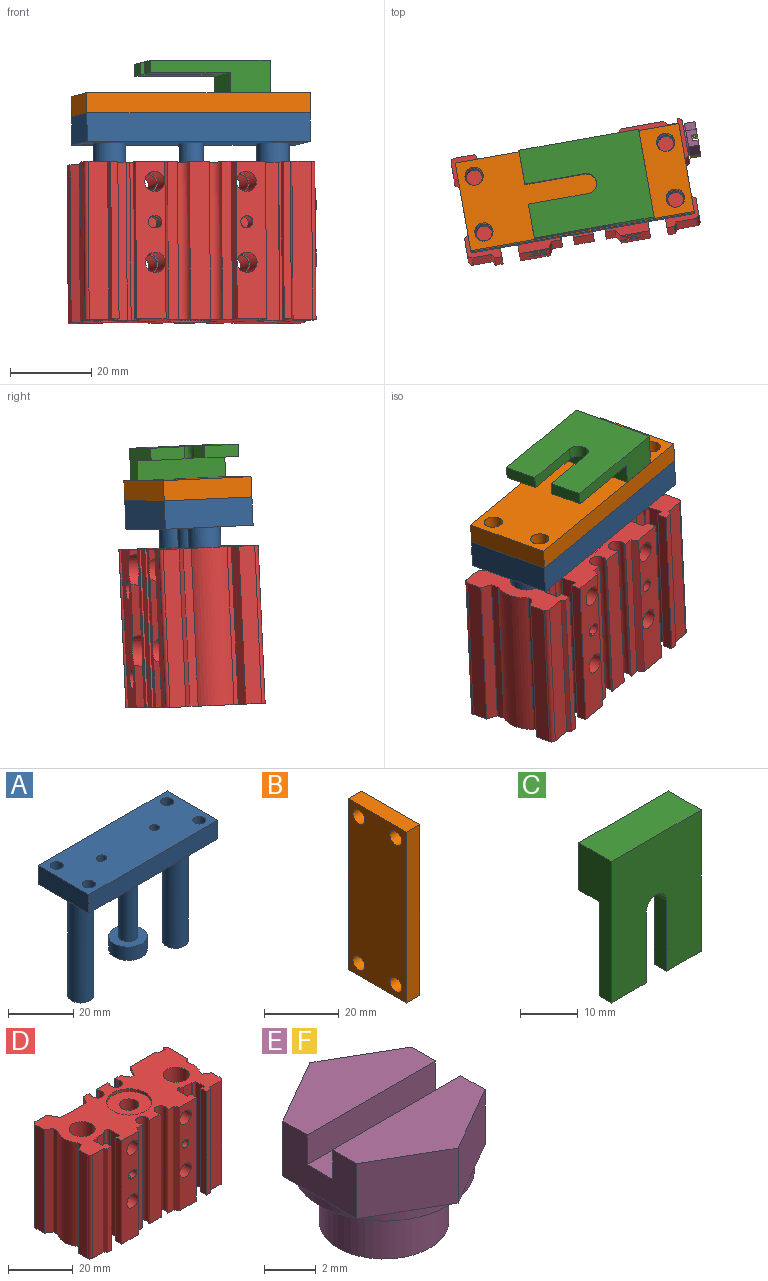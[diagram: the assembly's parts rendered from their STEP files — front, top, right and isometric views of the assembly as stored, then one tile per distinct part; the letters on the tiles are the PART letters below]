
ASSEMBLY  parts=6 mates=5
PART A: 30 faces, bbox 56x22x47.5 mm
  f0: plane 22x7mm, normal (-1,0,0), area 154mm2, adj f1,f3,f4,f5
  f1: plane 56x7mm, normal (0,-1,0), area 392mm2, adj f0,f2,f4,f5
  f2: plane 22x7mm, normal (1,0,0), area 154mm2, adj f1,f3,f4,f5
  f3: plane 56x7mm, normal (0,1,0), area 392mm2, adj f0,f2,f4,f5
  f4: plane 56x22mm, normal (0,0,1), area 1166.1mm2, adj f0,f1,f2,f3,f14,f18,f19,f20
  f5: plane 56x22mm, normal (0,0,-1), area 1052.9mm2, adj f0,f1,f2,f3,f6,f10,f12,f18
  f6: cylinder r=3mm len=28mm, axis (0,0,1), area 527.8mm2, adj f5,f8
  f7: cylinder r=5.95mm len=11.9mm, axis (0,0,-1), area 186.9mm2, adj f8,f9
  f8: plane 11.9x11.9mm, normal (0,0,1), area 82.9mm2, adj f6,f7
  f9: plane 11.9x11.9mm, normal (0,0,-1), area 111.2mm2, adj f7
  f10: cylinder r=4mm len=40mm, axis (0,0,1), area 1005.3mm2, adj f5,f16
  f11: plane 7x7mm, normal (0,0,-1), area 38.5mm2, adj f16
  f12: cylinder r=4mm len=40mm, axis (0,0,1), area 1005.3mm2, adj f5,f17
  f13: plane 7x7mm, normal (0,0,-1), area 38.5mm2, adj f17
  f14: cylinder r=1.5mm len=6mm, axis (0,0,1), area 56.5mm2, adj f4,f15
  f15: plane 3x3mm, normal (0,0,1), area 7.1mm2, adj f14
  f16: cone r=3.5mm half-angle=45deg, axis (0,0,1), area 16.7mm2, adj f10,f11
  f17: cone r=3.5mm half-angle=45deg, axis (0,0,1), area 16.7mm2, adj f12,f13
  f18: cylinder r=2mm len=7mm, axis (0,0,1), area 88mm2, adj f4,f5
  f19: cylinder r=2mm len=7mm, axis (0,0,1), area 88mm2, adj f4,f5
  f20: cylinder r=2mm len=7mm, axis (0,0,1), area 88mm2, adj f4,f5
  f21: cylinder r=2mm len=7mm, axis (0,0,1), area 88mm2, adj f4,f5
  f22: plane 3x0.5mm, normal (0,1,0), area 1.5mm2, adj f4,f24,f25,f26,f27
  f23: plane 3x0.5mm, normal (0,-1,0), area 1.5mm2, adj f4,f24,f25,f26,f27
  f24: plane 3x1.75mm, normal (0,0,1), area 0.8mm2, adj f22,f23,f27,f29
  f25: plane 3x1.75mm, normal (0,0,1), area 0.8mm2, adj f22,f23,f26,f29
  f26: cylinder r=1.5mm len=3mm, axis (0,0,1), area 14.1mm2, adj f4,f22,f23,f25
  f27: cylinder r=1.5mm len=3mm, axis (0,0,1), area 14.1mm2, adj f4,f22,f23,f24
  f28: plane 3x3mm, normal (0,0,1), area 7.1mm2, adj f29
  f29: cylinder r=1.5mm len=3mm, axis (0,0,1), area 28.3mm2, adj f24,f25,f28
PART B: 10 faces, bbox 5x22x56 mm
  f0: plane 56x5mm, normal (0,-1,0), area 280mm2, adj f1,f3,f4,f5
  f1: plane 22x5mm, normal (0,0,-1), area 110mm2, adj f0,f2,f4,f5
  f2: plane 56x5mm, normal (0,1,0), area 280mm2, adj f1,f3,f4,f5
  f3: plane 22x5mm, normal (0,0,1), area 110mm2, adj f0,f2,f4,f5
  f4: plane 56x22mm, normal (1,0,0), area 1168.4mm2, adj f0,f1,f2,f3,f6,f7,f8,f9
  f5: plane 56x22mm, normal (-1,0,0), area 1168.4mm2, adj f0,f1,f2,f3,f6,f7,f8,f9
  f6: cylinder r=2.25mm len=5mm, axis (1,0,0), area 70.7mm2, adj f4,f5
  f7: cylinder r=2.25mm len=5mm, axis (1,0,0), area 70.7mm2, adj f4,f5
  f8: cylinder r=2.25mm len=5mm, axis (1,0,0), area 70.7mm2, adj f4,f5
  f9: cylinder r=2.25mm len=5mm, axis (1,0,0), area 70.7mm2, adj f4,f5
PART C: 12 faces, bbox 22x8x30 mm
  f0: plane 8.5x3mm, normal (0,0,-1), area 25.5mm2, adj f1,f2,f8,f11
  f1: plane 30x22mm, normal (0,-1,0), area 575.2mm2, adj f0,f3,f6,f7,f8,f9,f10,f11
  f2: plane 22x20mm, normal (0,1,0), area 355.2mm2, adj f0,f3,f4,f7,f8,f9,f10,f11
  f3: plane 8.5x3mm, normal (0,0,-1), area 25.5mm2, adj f1,f2,f7,f9
  f4: plane 22x5mm, normal (0,0,-1), area 110mm2, adj f2,f5,f7,f8
  f5: plane 22x10mm, normal (0,1,0), area 220mm2, adj f4,f6,f7,f8
  f6: plane 22x8mm, normal (0,0,1), area 176mm2, adj f1,f5,f7,f8
  f7: plane 30x8mm, normal (1,0,0), area 140mm2, adj f1,f2,f3,f4,f5,f6
  f8: plane 30x8mm, normal (-1,0,0), area 140mm2, adj f0,f1,f2,f4,f5,f6
  f9: plane 15x3mm, normal (-1,0,0), area 45mm2, adj f1,f2,f3,f10
  f10: cylinder r=2.5mm len=5mm, axis (0,-1,0), area 23.6mm2, adj f1,f2,f9,f11
  f11: plane 15x3mm, normal (1,0,0), area 45mm2, adj f0,f1,f2,f10
PART D: 162 faces, bbox 58x26x39 mm
  f0: plane 12x12mm, normal (0,0,1), area 113.1mm2, adj f1
  f1: cylinder r=6mm len=15mm, axis (0,0,1), area 565.5mm2, adj f0,f2
  f2: plane 12x12mm, normal (0,0,-1), area 84.8mm2, adj f1,f3
  f3: cylinder r=3mm len=11mm, axis (0,0,1), area 207.3mm2, adj f2,f92
  f4: plane 4x2.31mm, normal (-0.87,0.5,0), area 5.3mm2, adj f6,f14,f83,f121
  f5: plane 13.07x4mm, normal (-0.87,0.5,0), area 56.8mm2, adj f7,f83,f116,f121
  f6: plane 1.52x1.44mm, normal (0,1,0), area 1.8mm2, adj f4,f14,f86,f121
  f7: plane 12.88x1.52mm, normal (0,1,0), area 18.7mm2, adj f5,f8,f116,f121
  f8: plane 16.13x2.9mm, normal (0.87,0.5,0), area 47.5mm2, adj f7,f17,f116,f121
  f9: plane 12.06x2.9mm, normal (0.87,0.5,0), area 37.1mm2, adj f13,f17,f85,f116
  f10: plane 16.13x2.9mm, normal (-0.87,0.5,0), area 47.5mm2, adj f87,f89,f106,f111
  f11: plane 3.06x2.9mm, normal (-0.87,0.5,0), area 7mm2, adj f14,f87,f89,f106
  f12: plane 39x2.5mm, normal (0,-1,0), area 97.5mm2, adj f13,f14,f54,f104
  f13: plane 58x26mm, normal (0,0,-1), area 919.8mm2, adj f9,f12,f15,f16,f17,f18,f20,f22
  f14: plane 58x26mm, normal (0,0,1), area 947.9mm2, adj f4,f6,f11,f12,f15,f16,f17,f30
  f15: plane 39x2.5mm, normal (0,-1,0), area 97.5mm2, adj f13,f14,f56,f100
  f16: plane 39x5mm, normal (0,1,0), area 195mm2, adj f13,f14,f95,f97
  f17: plane 39x2.5mm, normal (0,1,0), area 94.9mm2, adj f8,f9,f13,f14,f86,f98,f116,f121
  f18: cylinder r=6mm len=12mm, axis (0,0,-1), area 37.7mm2, adj f13,f19
  f19: plane 12x12mm, normal (0,0,-1), area 113.1mm2, adj f18
  f20: cylinder r=1.5mm len=6mm, axis (0,0,-1), area 56.5mm2, adj f13,f21
  f21: plane 3x3mm, normal (0,0,-1), area 7.1mm2, adj f20
  f22: plane 3x1.5mm, normal (0,-1,0), area 4.5mm2, adj f13,f24,f25,f26,f27
  f23: plane 3x1.5mm, normal (0,1,0), area 4.5mm2, adj f13,f24,f25,f26,f27
  f24: plane 3x2.25mm, normal (0,0,-1), area 2.3mm2, adj f22,f23,f26,f29
  f25: plane 3x2.25mm, normal (0,0,-1), area 2.3mm2, adj f22,f23,f27,f29
  f26: cylinder r=1.5mm len=3mm, axis (0,0,-1), area 14.1mm2, adj f13,f22,f23,f24
  f27: cylinder r=1.5mm len=3mm, axis (0,0,-1), area 14.1mm2, adj f13,f22,f23,f25
  f28: plane 3x3mm, normal (0,0,-1), area 7.1mm2, adj f29
  f29: cylinder r=1.5mm len=3mm, axis (0,0,-1), area 28.3mm2, adj f24,f25,f28
  f30: cylinder r=1mm len=39mm, axis (0,0,1), area 61.3mm2, adj f13,f14,f31,f91
  f31: plane 39x4mm, normal (-1,0,0), area 156mm2, adj f13,f14,f30,f32
  f32: plane 39x2.5mm, normal (-0.5,-0.87,0), area 112.6mm2, adj f13,f14,f31,f33
  f33: plane 39x2.06mm, normal (-1,0,0), area 80.2mm2, adj f13,f14,f32,f34
  f34: cylinder r=7.5mm len=39mm, axis (0,0,1), area 376.4mm2, adj f13,f14,f33,f35
  f35: plane 39x1.06mm, normal (-1,0,0), area 41.2mm2, adj f13,f14,f34,f36
  f36: plane 39x2.5mm, normal (-0.5,0.87,0), area 112.6mm2, adj f13,f14,f35,f37
  f37: plane 39x4mm, normal (-1,0,0), area 156mm2, adj f13,f14,f36,f38
  f38: cylinder r=1mm len=39mm, axis (0,0,1), area 61.3mm2, adj f13,f14,f37,f39
  f39: plane 39x4.92mm, normal (0,-1,0), area 192mm2, adj f13,f14,f38,f40
  f40: plane 39x1mm, normal (-0.87,-0.5,0), area 45mm2, adj f13,f14,f39,f41
  f41: plane 39x1.8mm, normal (0,-1,0), area 70.2mm2, adj f13,f14,f40,f42
  f42: plane 39x2.5mm, normal (1,0,0), area 97.5mm2, adj f13,f14,f41,f43
  f43: plane 39x1.5mm, normal (0,1,0), area 58.5mm2, adj f13,f14,f42,f44
  f44: plane 39x3.7mm, normal (1,0,0), area 144.3mm2, adj f13,f14,f43,f45
  f45: plane 39x1.5mm, normal (0,-1,0), area 58.5mm2, adj f13,f14,f44,f46
  f46: plane 39x0.5mm, normal (1,0,0), area 19.5mm2, adj f13,f14,f45,f47
  f47: plane 39x3.25mm, normal (0,-1,0), area 126.8mm2, adj f13,f14,f46,f48
  f48: cylinder r=7mm len=39mm, axis (0,0,1), area 48.3mm2, adj f13,f14,f47,f49
  f49: cylinder r=1mm len=39mm, axis (0,0,1), area 85.8mm2, adj f13,f14,f48,f50
  f50: plane 39x4.03mm, normal (-1,0,0), area 157mm2, adj f13,f14,f49,f51
  f51: plane 39x1.5mm, normal (0,1,0), area 58.5mm2, adj f13,f14,f50,f52
  f52: plane 39x2.5mm, normal (-1,0,0), area 97.5mm2, adj f13,f14,f51,f53
  f53: plane 39x7.38mm, normal (0,-1,0), area 239.8mm2, adj f13,f14,f52,f54,f110,f115,f128,f129
  f54: plane 39x1.6mm, normal (0.87,-0.5,0), area 72.1mm2, adj f12,f13,f14,f53
  f55: plane 39x5mm, normal (0,-1,0), area 195mm2, adj f13,f14,f101,f103
  f56: plane 39x1.6mm, normal (-0.87,-0.5,0), area 72.1mm2, adj f13,f14,f15,f57
  f57: plane 39x7.38mm, normal (0,-1,0), area 241.3mm2, adj f13,f14,f56,f58,f120,f125,f126
  f58: plane 39x2.5mm, normal (1,0,0), area 97.5mm2, adj f13,f14,f57,f59
  f59: plane 39x1.5mm, normal (0,1,0), area 58.5mm2, adj f13,f14,f58,f60
  f60: plane 39x4.03mm, normal (1,0,0), area 157mm2, adj f13,f14,f59,f61
  f61: cylinder r=1mm len=39mm, axis (0,0,1), area 85.8mm2, adj f13,f14,f60,f62
  f62: cylinder r=7mm len=39mm, axis (0,0,1), area 48.3mm2, adj f13,f14,f61,f63
  f63: plane 39x3.25mm, normal (0,-1,0), area 126.8mm2, adj f13,f14,f62,f64
  f64: plane 39x0.5mm, normal (-1,0,0), area 19.5mm2, adj f13,f14,f63,f65
  f65: plane 39x1.5mm, normal (0,-1,0), area 58.5mm2, adj f13,f14,f64,f66
  f66: plane 39x3.7mm, normal (-1,0,0), area 144.3mm2, adj f13,f14,f65,f67
  f67: plane 39x1.5mm, normal (0,1,0), area 58.5mm2, adj f13,f14,f66,f68
  f68: plane 39x2.5mm, normal (-1,0,0), area 97.5mm2, adj f13,f14,f67,f69
  f69: plane 39x1.8mm, normal (0,-1,0), area 70.2mm2, adj f13,f14,f68,f70
  f70: plane 39x1mm, normal (0.87,-0.5,0), area 45mm2, adj f13,f14,f69,f71
  f71: plane 39x4.92mm, normal (0,-1,0), area 192mm2, adj f13,f14,f70,f72
  f72: cylinder r=1mm len=39mm, axis (0,0,1), area 61.3mm2, adj f13,f14,f71,f73
  f73: plane 39x4mm, normal (1,0,0), area 156mm2, adj f13,f14,f72,f74
  f74: plane 39x2.5mm, normal (0.5,0.87,0), area 112.6mm2, adj f13,f14,f73,f75
  f75: plane 39x1.06mm, normal (1,0,0), area 41.2mm2, adj f13,f14,f74,f76
  f76: cylinder r=7.5mm len=39mm, axis (0,0,1), area 293.6mm2, adj f13,f14,f75,f77
  f77: plane 39x1.48mm, normal (0.5,-0.87,0), area 66.7mm2, adj f13,f14,f76,f78
  f78: plane 39x8.5mm, normal (1,0,0), area 292.2mm2, adj f13,f14,f77,f79,f155,f159
  f79: cylinder r=1mm len=39mm, axis (0,0,1), area 61.3mm2, adj f13,f14,f78,f80
  f80: plane 39x1mm, normal (-0.94,0.34,0), area 41.5mm2, adj f13,f14,f79,f81
  f81: plane 39x2.44mm, normal (0,1,0), area 95mm2, adj f13,f14,f80,f82
  f82: plane 39x1mm, normal (0.82,0.57,0), area 47.6mm2, adj f13,f14,f81,f83
  f83: plane 39x11mm, normal (0,1,0), area 370.1mm2, adj f4,f5,f13,f14,f82,f84,f116,f121
  f84: plane 10.54x4mm, normal (-0.87,0.5,0), area 46.9mm2, adj f13,f83,f85,f116
  f85: plane 10.44x1.52mm, normal (0,1,0), area 15.4mm2, adj f9,f13,f84,f116
  f86: plane 3.06x2.9mm, normal (0.87,0.5,0), area 7mm2, adj f6,f14,f17,f121
  f87: plane 39x2.5mm, normal (0,1,0), area 94.9mm2, adj f10,f11,f13,f14,f88,f94,f106,f111
  f88: plane 12.06x2.9mm, normal (-0.87,0.5,0), area 37.1mm2, adj f13,f87,f89,f111
  f89: plane 39x11.02mm, normal (0,1,0), area 351.2mm2, adj f10,f11,f13,f14,f88,f90,f106,f111
  f90: plane 39x4mm, normal (0.87,0.5,0), area 180.1mm2, adj f13,f14,f89,f91
  f91: plane 39x5mm, normal (0,1,0), area 195mm2, adj f13,f14,f30,f90
  f92: plane 14x14mm, normal (0,0,1), area 125.7mm2, adj f3,f93
  f93: cylinder r=7mm len=14mm, axis (0,0,1), area 44mm2, adj f14,f92
  f94: plane 39x0.74mm, normal (1,0,0), area 28.8mm2, adj f13,f14,f87,f96
  f95: plane 39x0.74mm, normal (-1,0,0), area 28.8mm2, adj f13,f14,f16,f96
  f96: cylinder r=2.02mm len=39mm, axis (0,0,1), area 364.5mm2, adj f13,f14,f94,f95
  f97: plane 39x0.74mm, normal (1,0,0), area 28.8mm2, adj f13,f14,f16,f99
  f98: plane 39x0.74mm, normal (-1,0,0), area 28.8mm2, adj f13,f14,f17,f99
  f99: cylinder r=2.02mm len=39mm, axis (0,0,1), area 364.5mm2, adj f13,f14,f97,f98
  f100: plane 39x0.24mm, normal (-1,0,0), area 9.3mm2, adj f13,f14,f15,f102
  f101: plane 39x0.24mm, normal (1,0,0), area 9.3mm2, adj f13,f14,f55,f102
  f102: cylinder r=2.02mm len=39mm, axis (0,0,1), area 364.5mm2, adj f13,f14,f100,f101
  f103: plane 39x0.24mm, normal (-1,0,0), area 9.3mm2, adj f13,f14,f55,f105
  f104: plane 39x0.24mm, normal (1,0,0), area 9.3mm2, adj f12,f13,f14,f105
  f105: cylinder r=2.02mm len=39mm, axis (0,0,1), area 364.5mm2, adj f13,f14,f103,f104
  f106: cylinder r=4mm len=8mm, axis (0,1,0), area 31.8mm2, adj f10,f11,f87,f89,f107
  f107: plane 8x8mm, normal (0,1,0), area 35.7mm2, adj f106,f108
  f108: cylinder r=2.15mm len=11.5mm, axis (0,1,0), area 155.4mm2, adj f107,f109
  f109: plane 5x5mm, normal (0,-1,0), area 5.1mm2, adj f108,f110
  f110: cylinder r=2.5mm len=10mm, axis (0,1,0), area 157.1mm2, adj f53,f109
  f111: cylinder r=4mm len=8mm, axis (0,1,0), area 31.8mm2, adj f10,f87,f88,f89,f112
  f112: plane 8x8mm, normal (0,1,0), area 35.7mm2, adj f111,f113
  f113: cylinder r=2.15mm len=11.5mm, axis (0,1,0), area 155.4mm2, adj f112,f114
  f114: plane 5x5mm, normal (0,-1,0), area 5.1mm2, adj f113,f115
  f115: cylinder r=2.5mm len=10mm, axis (0,1,0), area 157.1mm2, adj f53,f114
  f116: cylinder r=4mm len=8mm, axis (0,1,0), area 75.2mm2, adj f5,f7,f8,f9,f17,f83,f84,f85
  f117: plane 8x8mm, normal (0,1,0), area 35.7mm2, adj f116,f118
  f118: cylinder r=2.15mm len=11.5mm, axis (0,1,0), area 155.4mm2, adj f117,f119
  f119: plane 5x5mm, normal (0,-1,0), area 5.1mm2, adj f118,f120
  f120: cylinder r=2.5mm len=10mm, axis (0,1,0), area 157.1mm2, adj f57,f119
  f121: cylinder r=4mm len=8mm, axis (0,1,0), area 75.2mm2, adj f4,f5,f6,f7,f8,f17,f83,f86
  f122: plane 8x8mm, normal (0,1,0), area 35.7mm2, adj f121,f123
  f123: cylinder r=2.15mm len=11.5mm, axis (0,1,0), area 155.4mm2, adj f122,f124
  f124: plane 5x5mm, normal (0,-1,0), area 5.1mm2, adj f123,f125
  f125: cylinder r=2.5mm len=10mm, axis (0,1,0), area 157.1mm2, adj f57,f124
  f126: cylinder r=1.5mm len=6mm, axis (0,-1,0), area 56.5mm2, adj f57,f127
  f127: plane 3x3mm, normal (0,-1,0), area 7.1mm2, adj f126
  f128: plane 3x0.5mm, normal (0,0,1), area 1.5mm2, adj f53,f130,f131,f132,f133
  f129: plane 3x0.5mm, normal (0,0,-1), area 1.5mm2, adj f53,f130,f131,f132,f133
  f130: plane 3x1.75mm, normal (0,-1,0), area 0.8mm2, adj f128,f129,f133,f135
  f131: plane 3x1.75mm, normal (0,-1,0), area 0.7mm2, adj f128,f129,f132,f135
  f132: cylinder r=1.5mm len=3mm, axis (0,-1,0), area 14.1mm2, adj f53,f128,f129,f131
  f133: cylinder r=1.5mm len=3mm, axis (0,-1,0), area 14.1mm2, adj f53,f128,f129,f130
  f134: plane 3x3mm, normal (0,-1,0), area 7.1mm2, adj f135
  f135: cylinder r=1.5mm len=3mm, axis (0,-1,0), area 28.3mm2, adj f130,f131,f134
  f136: cylinder r=2mm len=10mm, axis (0,0,-1), area 125.7mm2, adj f13,f137
  f137: plane 4x4mm, normal (0,0,-1), area 12.6mm2, adj f136
  f138: cylinder r=2mm len=10mm, axis (0,0,-1), area 125.7mm2, adj f13,f139
  f139: plane 4x4mm, normal (0,0,-1), area 12.6mm2, adj f138
  f140: cylinder r=2mm len=10mm, axis (0,0,-1), area 125.7mm2, adj f13,f141
  f141: plane 4x4mm, normal (0,0,-1), area 12.6mm2, adj f140
  f142: cylinder r=2mm len=10mm, axis (0,0,-1), area 125.7mm2, adj f13,f143
  f143: plane 4x4mm, normal (0,0,-1), area 12.6mm2, adj f142
  f144: cylinder r=2.5mm len=5mm, axis (0,1,0), area 47.1mm2, adj f83,f145
  f145: plane 5x5mm, normal (0,1,0), area 5.8mm2, adj f144,f146
  f146: cylinder r=2.1mm len=4.2mm, axis (0,1,0), area 26.4mm2, adj f145,f147
  f147: cone r=2.1mm half-angle=59deg, axis (0,1,0), area 16.2mm2, adj f146
  f148: cylinder r=2.5mm len=5mm, axis (0,1,0), area 47.1mm2, adj f83,f149
  f149: plane 5x5mm, normal (0,1,0), area 5.8mm2, adj f148,f150
  f150: cylinder r=2.1mm len=4.2mm, axis (0,1,0), area 26.4mm2, adj f149,f151
  f151: cone r=2.1mm half-angle=59deg, axis (0,1,0), area 16.2mm2, adj f150
  f152: cone r=0mm half-angle=59deg, axis (1,0,0), area 16.2mm2, adj f153
  f153: cylinder r=2.1mm len=4.2mm, axis (1,0,0), area 26.4mm2, adj f152,f154
  f154: plane 5x5mm, normal (1,0,0), area 5.8mm2, adj f153,f155
  f155: cylinder r=2.5mm len=5mm, axis (1,0,0), area 47.1mm2, adj f78,f154
  f156: cone r=0mm half-angle=59deg, axis (1,0,0), area 16.2mm2, adj f157
  f157: cylinder r=2.1mm len=4.2mm, axis (1,0,0), area 26.4mm2, adj f156,f158
  f158: plane 5x5mm, normal (1,0,0), area 5.8mm2, adj f157,f159
  f159: cylinder r=2.5mm len=5mm, axis (1,0,0), area 47.1mm2, adj f78,f158
  f160: cylinder r=4mm len=39mm, axis (0,0,-1), area 980.2mm2, adj f13,f14
  f161: cylinder r=4mm len=39mm, axis (0,0,-1), area 980.2mm2, adj f13,f14
PART E: 21 faces, bbox 7x8.1x5.5 mm
  f0: plane 7x3.34mm, normal (0,0,1), area 16.3mm2, adj f12,f13,f14,f15,f18
  f1: plane 5x5mm, normal (0,0,-1), area 19.6mm2, adj f2
  f2: cylinder r=2.5mm len=5mm, axis (0,0,-1), area 39.3mm2, adj f1,f4
  f3: cylinder r=3.5mm len=7mm, axis (0,0,-1), area 8.8mm2, adj f4,f5,f6,f7,f8,f9,f10
  f4: plane 7x7mm, normal (0,0,-1), area 18.8mm2, adj f2,f3
  f5: plane 3.03x1.75mm, normal (0,0,-1), area 0.7mm2, adj f3,f12,f13
  f6: plane 3.5x1.01mm, normal (0,0,-1), area 0.7mm2, adj f3,f13,f14
  f7: plane 3.03x1.75mm, normal (0,0,-1), area 0.7mm2, adj f3,f14,f15
  f8: plane 3.03x1.75mm, normal (0,0,-1), area 0.7mm2, adj f3,f15,f16
  f9: plane 3.5x1.01mm, normal (0,0,-1), area 0.7mm2, adj f3,f11,f16
  f10: plane 3.03x1.75mm, normal (0,0,-1), area 0.7mm2, adj f3,f11,f12
  f11: plane 3.5x2.6mm, normal (0.5,-0.87,0), area 10.5mm2, adj f9,f10,f12,f16,f17
  f12: plane 4.04x2.6mm, normal (1,0,0), area 8.5mm2, adj f0,f5,f10,f11,f13,f17,f18,f19
  f13: plane 3.5x2.6mm, normal (0.5,0.87,0), area 10.5mm2, adj f0,f5,f6,f12,f14
  f14: plane 3.5x2.6mm, normal (-0.5,0.87,0), area 10.5mm2, adj f0,f6,f7,f13,f15
  f15: plane 4.04x2.6mm, normal (-1,0,0), area 8.5mm2, adj f0,f7,f8,f14,f16,f17,f18,f19
  f16: plane 3.5x2.6mm, normal (-0.5,-0.87,0), area 10.5mm2, adj f8,f9,f11,f15,f17
  f17: plane 7x3.34mm, normal (0,0,1), area 16.3mm2, adj f11,f12,f15,f16,f20
  f18: plane 7x1.4mm, normal (0,-1,0), area 9.8mm2, adj f0,f12,f15,f19
  f19: plane 7x1.4mm, normal (0,0,1), area 9.8mm2, adj f12,f15,f18,f20
  f20: plane 7x1.4mm, normal (0,1,0), area 9.8mm2, adj f12,f15,f17,f19
PART F: same geometry as E
PLACE A rot(axis=(-0.25,-0.02,0.97),10.3deg) t=(11.66,79.01,42.12)mm
PLACE B rot(axis=(0.71,0.05,-0.7),171.1deg) t=(37.23,95.23,53.62)mm
PLACE C rot(axis=(-0.65,0.52,-0.55),115.8deg) t=(-2.22,88.64,61.61)mm
PLACE D rot(axis=(-0.25,-0.02,0.97),10.3deg) t=(11.85,77.93,17.65)mm
PLACE E rot(axis=(-0.11,0.99,0.06),90.2deg) t=(38.95,91.26,26.78)mm
PLACE F rot(axis=(-0.11,0.99,0.06),90.2deg) t=(39.05,90.68,13.79)mm
MATE fastened E.f2 <-> D.f153  axis (-0.98,-0.17,0) through (38.95,91.26,26.78)mm
MATE fastened F.f2 <-> D.f157  axis (-0.98,-0.17,0) through (39.05,90.68,13.79)mm
MATE slider A.f6 <-> D.f1  axis (-0.01,0.04,1) through (11.77,78.4,28.14)mm
MATE fastened A.f4 <-> B.f4  axis (-0.01,0.04,1) through (-15.97,74.46,49.12)mm
MATE fastened C.f5 <-> B.f5  axis (0.01,-0.04,-1) through (29.29,82.67,54.11)mm
